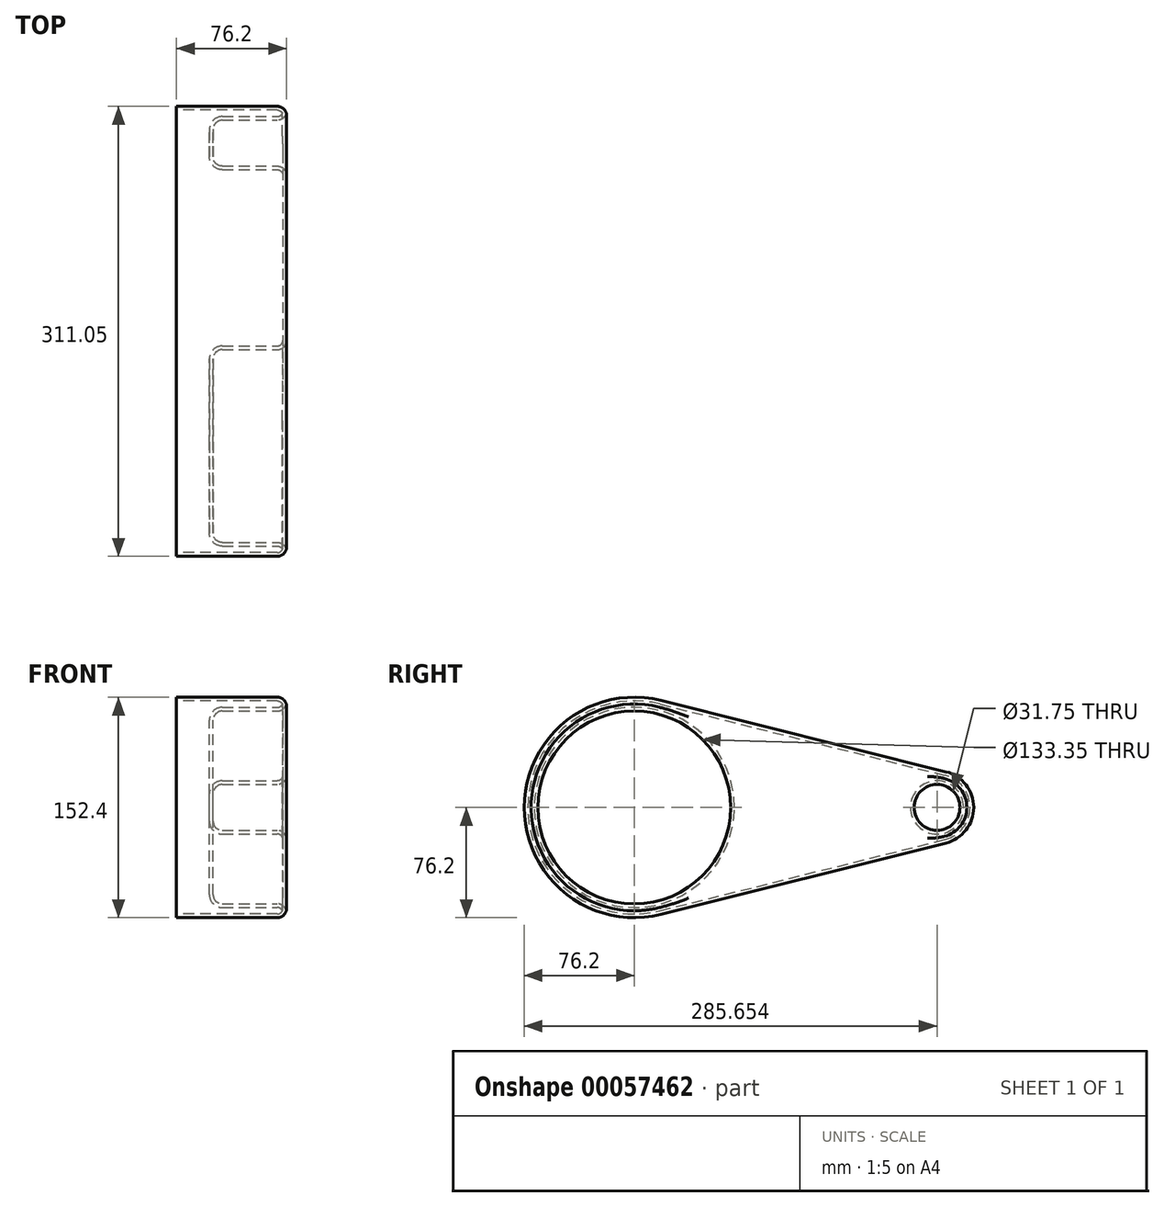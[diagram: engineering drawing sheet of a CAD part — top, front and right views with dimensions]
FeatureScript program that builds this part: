
annotation { "Feature Type Name" : "Feature", "Feature Type Description" : "" }
export const myFeature = defineFeature(function(context is Context, id is Id, definition is map)
    precondition{}
    {
        {
            var Q0;
            Q0=qCreatedBy(makeId("Right.planeOp"),FACE);
            var sketch = newSketch(context, id + "F0", { "sketchPlane" : qUnion([Q0])});
            skCircle(sketch, "E0", {"center": v(0, 0) * mm, "radius": 76.2 * mm});
            skCircle(sketch, "E1", {"center": v(209.45, 0) * mm, "radius": 25.4 * mm});
            skLineSegment(sketch, "E2", {"start": v(18.48, 73.92) * mm, "end": v(215.61, 24.64) * mm});
            skLineSegment(sketch, "E3", {"start": v(18.48, -73.92) * mm, "end": v(215.61, -24.64) * mm});
            skSolve(sketch);
        }
        {
            var Q0;
            {var subQ0=sQuery(id+"F0.wireOp",EDGE,"E0");var subQ1=makeQuery(id+"F0.imprint","INTERSECT",VERTEX,{"derivedFrom":[subQ0,sQuery(id+"F0.wireOp",EDGE,"E2")]});Q0=makeQuery(id+"F0.imprint","IMPRINT",FACE,{"disambiguationData":[TD([[makeQuery(id+"F0.imprint","IMPRINT",EDGE,{"disambiguationData":[TD([[subQ1,-1.0]])],"derivedFrom":subQ0}),1.0]])]});}
            var Q1;
            {var subQ0=sQuery(id+"F0.wireOp",EDGE,"E2");Q1=makeQuery(id+"F0.imprint","IMPRINT",FACE,{"disambiguationData":[TD([[makeQuery(id+"F0.imprint","IMPRINT",EDGE,{"derivedFrom":subQ0}),-1.0]])]});}
            var Q2;
            {var subQ0=sQuery(id+"F0.wireOp",EDGE,"E1");var subQ1=makeQuery(id+"F0.imprint","INTERSECT",VERTEX,{"derivedFrom":[subQ0,sQuery(id+"F0.wireOp",EDGE,"E2")]});Q2=makeQuery(id+"F0.imprint","IMPRINT",FACE,{"disambiguationData":[TD([[makeQuery(id+"F0.imprint","IMPRINT",EDGE,{"disambiguationData":[TD([[subQ1,-1.0]])],"derivedFrom":subQ0}),1.0]])]});}
            extrude(context, id + "F1", {"entities" : qUnion([Q0, Q1, Q2]), "depth" : 76.2 * mm});
        }
        {
            var Q0;
            Q0=makeQuery(id+"F1.opExtrude","CAP_FACE",FACE,{"disambiguationData":[OSD([sQuery(id+"F0.wireOp",EDGE,"E0"),sQuery(id+"F0.wireOp",EDGE,"E1"),sQuery(id+"F0.wireOp",EDGE,"E2"),sQuery(id+"F0.wireOp",EDGE,"E3")])],"isStart":false});
            var sketch = newSketch(context, id + "F2", { "sketchPlane" : qUnion([Q0])});
            skCircle(sketch, "E4", {"center": v(0, 0) * mm, "radius": 66.68 * mm});
            skCircle(sketch, "E5", {"center": v(209.45, 0) * mm, "radius": 15.88 * mm});
            skSolve(sketch);
        }
        {
            var Q0;
            Q0 = qSketchRegion(id + "F2", true);
            extrude(context, id + "F3", {"entities" : qUnion([Q0]), "operationType" : NewBodyOperationType.REMOVE, "oppositeDirection" : true, "depth" : 50.8 * mm});
        }
        {
            var Q0;
            Q0=makeQuery(id+"F1.opExtrude","CAP_FACE",FACE,{"disambiguationData":[OSD([sQuery(id+"F0.wireOp",EDGE,"E0"),sQuery(id+"F0.wireOp",EDGE,"E1"),sQuery(id+"F0.wireOp",EDGE,"E2"),sQuery(id+"F0.wireOp",EDGE,"E3")])],"isStart":false});
            var Q1;
            Q1=makeQuery(id+"F3.boolean.opBoolean","COPY",FACE,{"derivedFrom":makeQuery(id+"F3.opExtrude","CAP_FACE",FACE,{"disambiguationData":[OSD([sQuery(id+"F2.wireOp",EDGE,"E4")])],"isStart":false})});
            var Q2;
            Q2=makeQuery(id+"F3.boolean.opBoolean","COPY",FACE,{"derivedFrom":makeQuery(id+"F3.opExtrude","CAP_FACE",FACE,{"disambiguationData":[OSD([sQuery(id+"F2.wireOp",EDGE,"E5")])],"isStart":false})});
            fillet(context, id + "F4", {"entities" : qUnion([Q0, Q1, Q2]), "radius" : 6.35 * mm, "tangentPropagation" : true, "allowEdgeOverflow" : false});
        }
        {
            var Q0;
            Q0=makeQuery(id+"F1.opExtrude","CAP_FACE",FACE,{"disambiguationData":[OSD([sQuery(id+"F0.wireOp",EDGE,"E0"),sQuery(id+"F0.wireOp",EDGE,"E1"),sQuery(id+"F0.wireOp",EDGE,"E2"),sQuery(id+"F0.wireOp",EDGE,"E3")])],"isStart":true});
            shell(context, id + "F5", {"entities" : qUnion([Q0]), "thickness" : 2.54 * mm});
        }
    });
